# Revit family: Shower-Handshower_Kit-KOHLER-ALEO-K-31243T_1
name_source: partatom
category: Plumbing Fixtures
units: mm (PartAtom-declared; Revit-internal decimal feet)

## family parameters
Cut with Voids When Loaded = No
Host = Face
Maintain Annotation Orientation = No
OmniClass Number = 23.31.17.00
OmniClass Title = Showers
Part Type = Normal
Room Calculation Point = No
Round Connector Dimension = Use Diameter
Shared = No

## types (4) — shared parameters
ADA Compliant = No
Assembly Code = D2010700
CW Connection = Yes
Cold Water Inlet = Cold Water Inlet
Date Modified = 07/13/2022
Default Elevation = 36"
Drain Included = No
HW Connection = Yes
Height = 8 3/8"
Hot Water Inlet = Hot Water Inlet
Length = 7 9/16"
Manufacturer = Kohler Co.
Master Format 2014 = 22 42 23
Master Format 2014 Name = Residential Showers
Material = Premium Metal Construction
Pressure = 80.00 psi
Product Name = ALEO
URL = http://www.kohler.com.cn
Vent Connection = No
Waste Connection = No
Waste Water Outlet = Waste Water Outlet
WaterSense Certified = No

## per-type parameters (varying)
| type | Description | Finish | Flow Rate | Model | Product Documentation Link | Product Page URL | Type |
| 2.5 GPM, CP-Polished Chrome | Tank Side Diverter and Hand Shower | Kohler-Metal-CP-Polished_Chrome | 3 GPM | K-31243T-9-CP | https://files.kohler.com.cn | https://www.kohler.com.cn | 1 |
| 2.5 GPM, 2BL-Black | Tank Side Diverter and Hand Shower | KOHLER-Metal-2BL-Black | 3 GPM | K-31243T-9-2BL | https://files.kohler.com.cn | https://www.kohler.com.cn | 2 |
| 2.5 GPM, BL-Matte Black | Tank Side Diverter and Hand Shower | Kohler-Metal-BL-Matte_Black | 3 GPM | K-31243T-9-BL | https://files.kohler.com.cn | https://www.kohler.com.cn | 3 |
| 2.38 GPM, BL-Matte Black | S Diverter & Hand Shower | Kohler-Metal-BL-Matte_Black | 2 GPM | K-31243T-9E-BL |  |  | 4 |

## geometry (parser evidence)
native form markers: Sweep x8
no freeform markers — native parametric forms only
